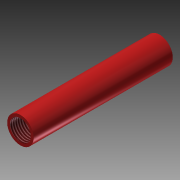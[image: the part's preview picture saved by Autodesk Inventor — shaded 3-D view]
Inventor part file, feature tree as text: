
AUTODESK INVENTOR PART (.ipt)
format: ipt  version: 2015 (Build 190159000, 159)  size: 81,408 bytes
history: native  units: mm
features: extrude x1, thread x1, sketch x1
ambient origin geometry x8: Origin, YZ Plane, XZ Plane, XY Plane, X Axis, Y Axis, Z Axis, Center Point
bodies: Solid1 (feature_tree)
feature tree (3):
  extrude  "Extrusion1"  Depth=10.0mm
  thread  "Thread1"  [1 undecoded]
  sketch  "Sketch1"  dims[d0=3.0mm d1=3.8mm d2=20.0mm d3=0.0mm d4=10.0mm d5=0.0mm]
note: 1 required parameter value undecoded (feature->parameter linkage not recoverable at this tier; creation-order binding heuristic only, values carry confidence <= 0.55)
